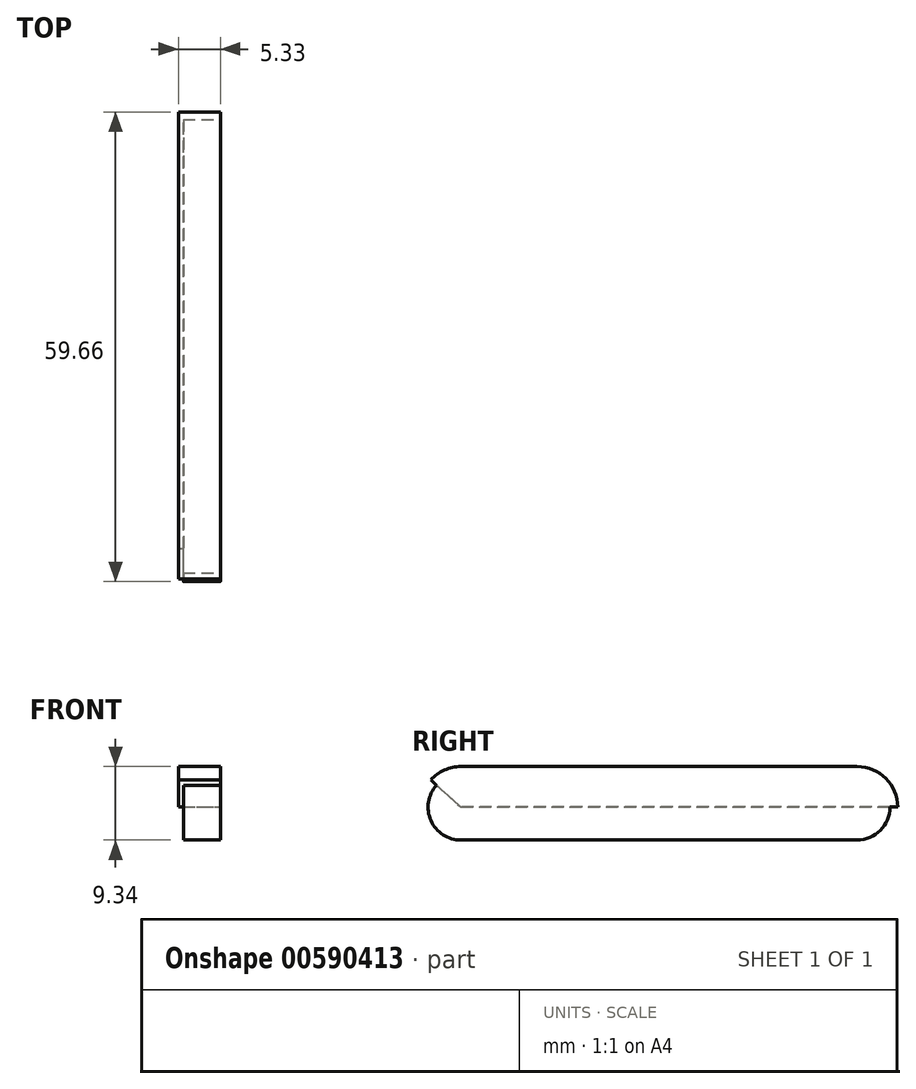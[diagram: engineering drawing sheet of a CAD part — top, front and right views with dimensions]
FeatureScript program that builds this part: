
annotation { "Feature Type Name" : "Feature", "Feature Type Description" : "" }
export const myFeature = defineFeature(function(context is Context, id is Id, definition is map)
    precondition{}
    {
        {
            var Q0;
            Q0=qCreatedBy(makeId("Right.planeOp"),FACE);
            var sketch = newSketch(context, id + "F0", { "sketchPlane" : qUnion([Q0])});
            skLineSegment(sketch, "E0", {"start": v(0, 0) * mm, "end": v(-50.32, 0) * mm});
            skLineSegment(sketch, "E1", {"start": v(-50.32, 0) * mm, "end": v(-50.32, 5.16) * mm});
            skLineSegment(sketch, "E2", {"start": v(-50.32, 5.16) * mm, "end": v(0, 5.16) * mm});
            skLineSegment(sketch, "E3", {"start": v(0, 5.16) * mm, "end": v(0, 0) * mm});
            skArc(sketch, "E4", {"start": v(0, 5.16) * mm, "mid": v(3.65, 3.65) * mm, "end": v(5.16, 0) * mm});
            skArc(sketch, "E5", {"start": v(-50.32, 5.16) * mm, "mid": v(-52.42, 4.7) * mm, "end": v(-54.16, 3.44) * mm});
            skLineSegment(sketch, "E6", {"start": v(-54.16, 3.44) * mm, "end": v(-50.32, 0) * mm});
            skLineSegment(sketch, "E7", {"start": v(0, 0) * mm, "end": v(5.16, 0) * mm});
            skSolve(sketch);
        }
        {
            var Q0;
            Q0=makeQuery(id+"F0.imprint","IMPRINT",FACE,{"disambiguationData":[TD([[makeQuery(id+"F0.imprint","IMPRINT",EDGE,{"derivedFrom":sQuery(id+"F0.wireOp",EDGE,"E3")}),1.0]])]});
            var Q1;
            Q1=makeQuery(id+"F0.imprint","IMPRINT",FACE,{"disambiguationData":[TD([[makeQuery(id+"F0.imprint","IMPRINT",EDGE,{"derivedFrom":sQuery(id+"F0.wireOp",EDGE,"E0")}),-1.0]])]});
            var Q2;
            Q2=makeQuery(id+"F0.imprint","IMPRINT",FACE,{"disambiguationData":[TD([[makeQuery(id+"F0.imprint","IMPRINT",EDGE,{"derivedFrom":sQuery(id+"F0.wireOp",EDGE,"E1")}),1.0]])]});
            extrude(context, id + "F1", {"entities" : qUnion([Q0, Q1, Q2]), "oppositeDirection" : true, "depth" : 5.33 * mm, "offsetDistance" : 25.4 * mm});
        }
        {
            var Q0;
            Q0=qCreatedBy(makeId("Right.planeOp"),FACE);
            var sketch = newSketch(context, id + "F2", { "sketchPlane" : qUnion([Q0])});
            skLineSegment(sketch, "E8", {"start": v(0, 0) * mm, "end": v(0, -4.18) * mm});
            skLineSegment(sketch, "E9", {"start": v(0, 0) * mm, "end": v(-50.32, 0) * mm});
            skLineSegment(sketch, "E10", {"start": v(-50.32, 0) * mm, "end": v(-50.32, -4.18) * mm});
            skLineSegment(sketch, "E11", {"start": v(-50.32, -4.18) * mm, "end": v(0, -4.18) * mm});
            skLineSegment(sketch, "E12", {"start": v(-50.32, 0) * mm, "end": v(-53.44, 2.8) * mm});
            skLineSegment(sketch, "E13", {"start": v(0, 0) * mm, "end": v(4.2, 0) * mm});
            skArc(sketch, "E14", {"start": v(0, -4.18) * mm, "mid": v(2.96, -2.96) * mm, "end": v(4.18, 0) * mm});
            skArc(sketch, "E15", {"start": v(-50.32, -4.18) * mm, "mid": v(-54.14, -1.7) * mm, "end": v(-53.43, 2.8) * mm});
            skSolve(sketch);
        }
        {
            var Q0;
            Q0=makeQuery(id+"F2.imprint","IMPRINT",FACE,{"disambiguationData":[TD([[makeQuery(id+"F2.imprint","IMPRINT",EDGE,{"derivedFrom":sQuery(id+"F2.wireOp",EDGE,"E8")}),-1.0]])]});
            var Q1;
            {var subQ0=sQuery(id+"F2.wireOp",EDGE,"E8");Q1=makeQuery(id+"F2.imprint","IMPRINT",FACE,{"disambiguationData":[TD([[makeQuery(id+"F2.imprint","IMPRINT",EDGE,{"derivedFrom":subQ0}),1.0]])]});}
            var Q2;
            {var subQ0=sQuery(id+"F2.wireOp",EDGE,"E10");Q2=makeQuery(id+"F2.imprint","IMPRINT",FACE,{"disambiguationData":[TD([[makeQuery(id+"F2.imprint","IMPRINT",EDGE,{"derivedFrom":subQ0}),-1.0]])]});}
            extrude(context, id + "F3", {"entities" : qUnion([Q0, Q1, Q2]), "operationType" : NewBodyOperationType.ADD, "oppositeDirection" : true, "depth" : 4.7 * mm, "offsetDistance" : 25.4 * mm});
        }
    });
